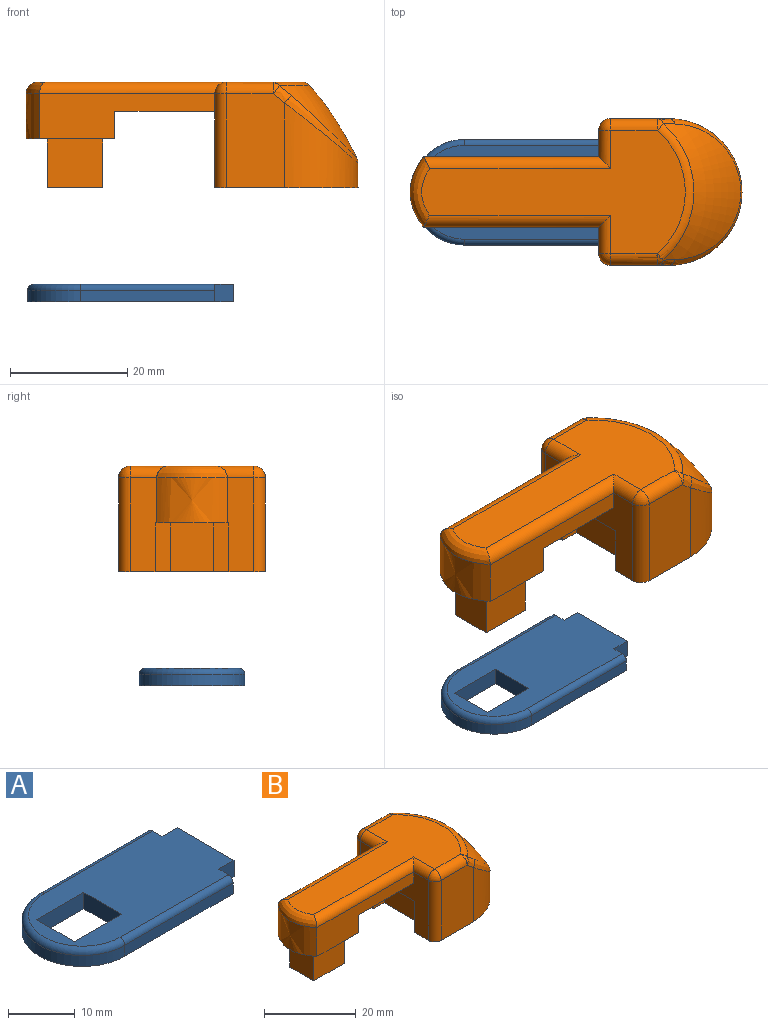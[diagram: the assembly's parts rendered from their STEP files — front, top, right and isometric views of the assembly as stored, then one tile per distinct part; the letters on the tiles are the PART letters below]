
ASSEMBLY  parts=2 mates=1
PART A: 17 faces, bbox 35.8x19.5x3 mm
  f0: plane 8x3mm, normal (1,0,0), area 24mm2, adj f1,f11,f12,f13
  f1: plane 10x3mm, normal (0,-1,0), area 30mm2, adj f0,f2,f12,f13
  f2: plane 8x3mm, normal (-1,0,0), area 24mm2, adj f1,f11,f12,f13
  f3: plane 3.2x3mm, normal (0,1,0), area 9.6mm2, adj f4,f10,f12,f13
  f4: plane 3x3mm, normal (1,0,0), area 8.8mm2, adj f3,f5,f12,f13,f16
  f5: plane 22.85x2mm, normal (0,1,0), area 45.7mm2, adj f4,f6,f13,f16
  f6: cylinder r=9mm len=18mm, axis (0,0,-1), area 56.5mm2, adj f5,f7,f13,f15
  f7: plane 22.85x2mm, normal (0,-1,0), area 45.7mm2, adj f6,f8,f13,f14
  f8: plane 3x3mm, normal (1,0,0), area 8.8mm2, adj f7,f9,f12,f13,f14
  f9: plane 3.2x3mm, normal (0,-1,0), area 9.6mm2, adj f8,f10,f12,f13
  f10: plane 12x3mm, normal (1,0,0), area 36mm2, adj f3,f9,f12,f13
  f11: plane 10x3mm, normal (0,1,0), area 30mm2, adj f0,f2,f12,f13
  f12: plane 34.05x16mm, normal (0,0,1), area 424.5mm2, adj f0,f1,f2,f3,f4,f8,f9,f10
  f13: plane 35.05x18mm, normal (0,0,-1), area 496.9mm2, adj f0,f1,f2,f3,f4,f5,f6,f7
  f14: cylinder r=1mm len=22.85mm, axis (-1,0,0), area 35.9mm2, adj f7,f8,f12,f15
  f15: torus R=8mm, axis (0,0,1), area 42.6mm2, adj f6,f12,f14,f16
  f16: cylinder r=1mm len=22.85mm, axis (1,0,0), area 35.9mm2, adj f4,f5,f12,f15
PART B: 44 faces, bbox 57.4x35.2x18.1 mm
  f0: plane 44.9x21mm, normal (0,0,1), area 490.6mm2, adj f1,f36,f37,f39,f40,f41,f42,f43
  f1: cylinder r=2mm len=6.5mm, axis (0,-1,0), area 17.3mm2, adj f0,f2,f35,f43
  f2: plane 21x16mm, normal (-1,0,0), area 195.4mm2, adj f1,f3,f5,f6,f7,f19,f20,f31
  f3: plane 8.3x3.2mm, normal (0,1,0), area 26.6mm2, adj f2,f4,f5,f7
  f4: plane 12.6x8.3mm, normal (-1,0,0), area 104.6mm2, adj f3,f5,f6,f7
  f5: plane 12.6x3.2mm, normal (0,0,-1), area 40.3mm2, adj f2,f3,f4,f6
  f6: plane 8.3x3.2mm, normal (0,-1,0), area 26.6mm2, adj f2,f4,f5,f7
  f7: plane 25x24.4mm, normal (0,0,-1), area 492.3mm2, adj f2,f3,f4,f6,f8,f15,f16,f17
  f8: plane 16x9.9mm, normal (0,1,0), area 157mm2, adj f7,f9,f16,f19,f36
  f9: bspline ~6.84x6.29mm, area 5.1mm2, adj f8,f10,f13,f14
  f10: bspline ~25.06x14.09mm, area 59.9mm2, adj f9,f11,f13,f16
  f11: bspline ~5.53x4.95mm, area 5.1mm2, adj f10,f12,f13,f15
  f12: sphere r=2mm, area 1.3mm2, adj f11,f37,f39
  f13: revolved ~35.19x13.22mm, area 294.2mm2, adj f9,f10,f11,f37
  f14: sphere r=2mm, area 1.9mm2, adj f9,f36,f37
  f15: plane 16x9.9mm, normal (0,-1,0), area 157mm2, adj f7,f11,f16,f33,f39
  f16: cylinder r=12.5mm len=25mm, axis (0,0,-1), area 315mm2, adj f7,f8,f10,f15
  f17: cylinder r=1.65mm len=12mm, axis (0,0,-1), area 124.4mm2, adj f7,f18
  f18: plane 3.3x3.3mm, normal (0,0,-1), area 8.6mm2, adj f17
  f19: cylinder r=2mm len=16mm, axis (0,0,-1), area 50.3mm2, adj f2,f7,f8,f35
  f20: plane 29.83x7.7mm, normal (0,1,0), area 149.6mm2, adj f2,f21,f29,f30,f31,f43
  f21: plane 16x12mm, normal (0,0,-1), area 102.6mm2, adj f20,f22,f26,f27,f28,f29,f30,f32
  f22: plane 8.3x7.4mm, normal (-1,0,0), area 61.4mm2, adj f21,f23,f26,f28
  f23: plane 9.4x7.4mm, normal (0,0,-1), area 61mm2, adj f22,f24,f26,f27,f28
  f24: cylinder r=1.65mm len=12mm, axis (0,0,-1), area 124.4mm2, adj f23,f25
  f25: plane 3.3x3.3mm, normal (0,0,-1), area 8.6mm2, adj f24
  f26: plane 9.4x8.3mm, normal (0,1,0), area 78mm2, adj f21,f22,f23,f27
  f27: plane 8.3x7.4mm, normal (1,0,0), area 61.4mm2, adj f21,f23,f26,f28
  f28: plane 9.4x8.3mm, normal (0,-1,0), area 78mm2, adj f21,f22,f23,f27
  f29: plane 12x4.7mm, normal (1,0,0), area 56.4mm2, adj f20,f21,f31,f32
  f30: extruded ~12x7.7mm, area 101mm2, adj f20,f21,f32,f42
  f31: plane 17.03x12mm, normal (0,0,-1), area 204.4mm2, adj f2,f20,f29,f32
  f32: plane 29.83x7.7mm, normal (0,-1,0), area 149.6mm2, adj f2,f21,f29,f30,f31,f41
  f33: cylinder r=2mm len=16mm, axis (0,0,-1), area 50.3mm2, adj f2,f7,f15,f34
  f34: sphere r=2mm, area 6.3mm2, adj f33,f39,f40
  f35: sphere r=2mm, area 8.6mm2, adj f1,f19,f36
  f36: cylinder r=2mm len=7.99mm, axis (1,0,0), area 25.1mm2, adj f0,f8,f14,f35
  f37: torus R=13.99mm, axis (0,0,-1), area 41.7mm2, adj f0,f12,f13,f14,f38
  f38: sphere r=2mm, area 0.1mm2, adj f37,f39
  f39: cylinder r=2mm len=7.99mm, axis (-1,0,0), area 25.1mm2, adj f0,f12,f15,f34,f38
  f40: cylinder r=2mm len=6.5mm, axis (0,-1,0), area 17.3mm2, adj f0,f2,f34,f41
  f41: cylinder r=2mm len=31.83mm, axis (-1,0,0), area 95.2mm2, adj f0,f32,f40,f42
  f42: bspline ~14.22x5.33mm, area 35mm2, adj f0,f30,f41,f43
  f43: cylinder r=2mm len=31.83mm, axis (-1,0,0), area 95.2mm2, adj f0,f1,f20,f42
PLACE A t=(14.24,6.31,-12.16)mm
PLACE B t=(13.94,6.31,7.31)mm
MATE slider A.f12 <-> B.f5  axis (0,0,1) through (6.94,6.31,-9.16)mm
